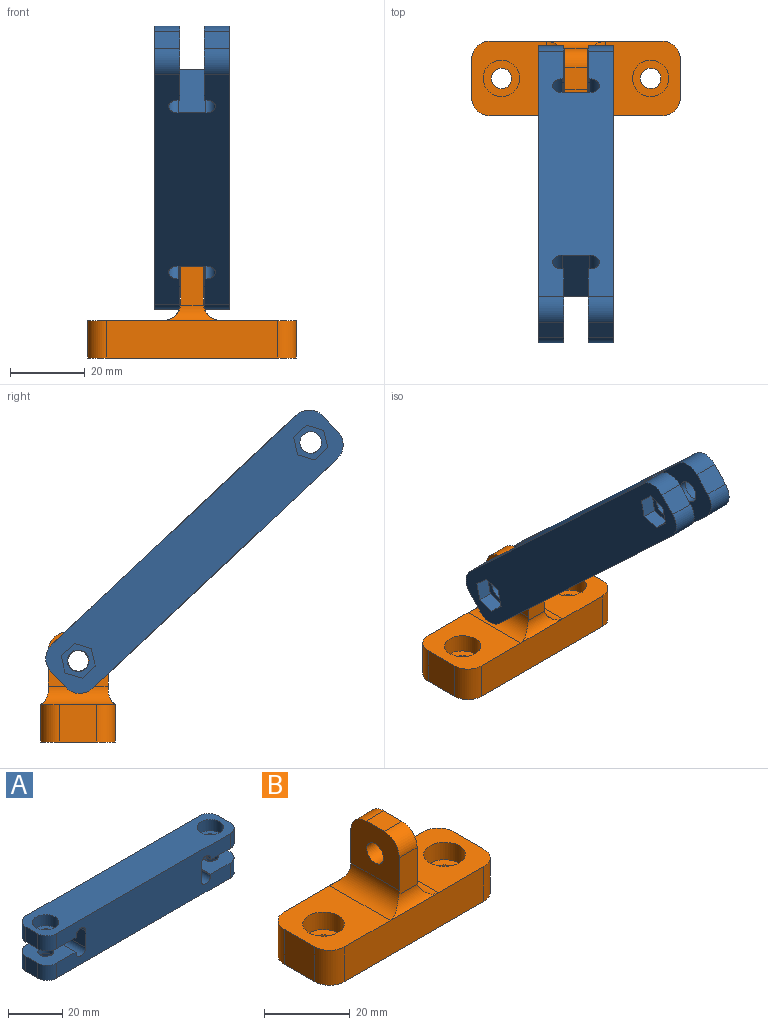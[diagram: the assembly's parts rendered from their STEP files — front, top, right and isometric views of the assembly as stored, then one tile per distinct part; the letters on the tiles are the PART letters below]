
ASSEMBLY  parts=2 mates=1
PART A: 52 faces, bbox 100x16x20 mm
  f0: plane 100x16mm, normal (0,0,-1), area 1459.2mm2, adj f4,f8,f9,f10,f11,f12,f14,f17
  f1: cylinder r=2.9mm len=5.8mm, axis (0,0,1), area 50.1mm2, adj f23,f51
  f2: cylinder r=2.9mm len=5.8mm, axis (0,0,1), area 50.1mm2, adj f18,f44
  f3: plane 6.75x6mm, normal (1,0,0), area 40.5mm2, adj f5,f6,f13,f27
  f4: plane 90x20mm, normal (0,1,0), area 1555.7mm2, adj f0,f5,f9,f13,f14,f15,f18,f19
  f5: cylinder r=5mm len=6.75mm, axis (0,0,1), area 53mm2, adj f3,f4,f13,f27
  f6: cylinder r=5mm len=6.75mm, axis (0,0,-1), area 53mm2, adj f3,f8,f13,f27
  f7: plane 6.75x6mm, normal (-1,0,0), area 40.5mm2, adj f13,f15,f16,f19
  f8: plane 90x20mm, normal (0,-1,0), area 1555.7mm2, adj f0,f6,f10,f13,f16,f17,f18,f19
  f9: cylinder r=5mm len=6.75mm, axis (0,0,-1), area 53mm2, adj f0,f4,f12,f18
  f10: cylinder r=5mm len=6.75mm, axis (0,0,1), area 53mm2, adj f0,f8,f12,f18
  f11: plane 6.75x6mm, normal (1,0,0), area 40.5mm2, adj f0,f14,f17,f23
  f12: plane 6.75x6mm, normal (-1,0,0), area 40.5mm2, adj f0,f9,f10,f18
  f13: plane 100x16mm, normal (0,0,1), area 1429.2mm2, adj f3,f4,f5,f6,f7,f8,f15,f16
  f14: cylinder r=5mm len=6.75mm, axis (0,0,1), area 53mm2, adj f0,f4,f11,f23
  f15: cylinder r=5mm len=6.75mm, axis (0,0,-1), area 53mm2, adj f4,f7,f13,f19
  f16: cylinder r=5mm len=6.75mm, axis (0,0,1), area 53mm2, adj f7,f8,f13,f19
  f17: cylinder r=5mm len=6.75mm, axis (0,0,-1), area 53mm2, adj f0,f8,f11,f23
  f18: plane 16x15mm, normal (0,0,1), area 202.8mm2, adj f2,f4,f8,f9,f10,f12,f22
  f19: plane 16x15mm, normal (0,0,-1), area 202.8mm2, adj f4,f7,f8,f15,f16,f20,f33
  f20: plane 16x0.5mm, normal (1,0,0), area 8mm2, adj f4,f8,f19,f36
  f21: plane 16x7.5mm, normal (-1,0,0), area 120mm2, adj f4,f8,f36,f37
  f22: plane 16x0.5mm, normal (1,0,0), area 8mm2, adj f4,f8,f18,f37
  f23: plane 16x15mm, normal (0,0,1), area 202.8mm2, adj f1,f4,f8,f11,f14,f17,f24
  f24: plane 16x0.5mm, normal (-1,0,0), area 8mm2, adj f4,f8,f23,f35
  f25: plane 16x7.5mm, normal (1,0,0), area 120mm2, adj f4,f8,f34,f35
  f26: plane 16x0.5mm, normal (-1,0,0), area 8mm2, adj f4,f8,f27,f34
  f27: plane 16x15mm, normal (0,0,-1), area 202.8mm2, adj f3,f4,f5,f6,f8,f26,f30
  f28: cylinder r=4.88mm len=9.75mm, axis (0,0,1), area 153.2mm2, adj f13,f29
  f29: plane 9.75x9.75mm, normal (0,0,1), area 48.2mm2, adj f28,f30
  f30: cylinder r=2.9mm len=5.8mm, axis (0,0,1), area 31.9mm2, adj f27,f29
  f31: cylinder r=4.88mm len=9.75mm, axis (0,0,1), area 153.2mm2, adj f13,f32
  f32: plane 9.75x9.75mm, normal (0,0,1), area 48.2mm2, adj f31,f33
  f33: cylinder r=2.9mm len=5.8mm, axis (0,0,1), area 31.9mm2, adj f19,f32
  f34: cylinder r=2.5mm len=16mm, axis (0,-1,0), area 125.7mm2, adj f4,f8,f25,f26
  f35: cylinder r=2.5mm len=16mm, axis (0,-1,0), area 125.7mm2, adj f4,f8,f24,f25
  f36: cylinder r=2.5mm len=16mm, axis (0,-1,0), area 125.7mm2, adj f4,f8,f20,f21
  f37: cylinder r=2.5mm len=16mm, axis (0,-1,0), area 125.7mm2, adj f4,f8,f21,f22
  f38: plane 4.15x4mm, normal (-0.87,-0.5,0), area 19.2mm2, adj f0,f39,f43,f44
  f39: plane 4.15x4mm, normal (-0.87,0.5,0), area 19.2mm2, adj f0,f38,f40,f44
  f40: plane 4.79x4mm, normal (0,1,0), area 19.2mm2, adj f0,f39,f41,f44
  f41: plane 4.15x4mm, normal (0.87,0.5,0), area 19.2mm2, adj f0,f40,f42,f44
  f42: plane 4.15x4mm, normal (0.87,-0.5,0), area 19.2mm2, adj f0,f41,f43,f44
  f43: plane 4.79x4mm, normal (0,-1,0), area 19.2mm2, adj f0,f38,f42,f44
  f44: plane 9.58x8.3mm, normal (0,0,-1), area 33.2mm2, adj f2,f38,f39,f40,f41,f42,f43
  f45: plane 4.79x4mm, normal (0,1,0), area 19.2mm2, adj f0,f46,f50,f51
  f46: plane 4.15x4mm, normal (0.87,0.5,0), area 19.2mm2, adj f0,f45,f47,f51
  f47: plane 4.15x4mm, normal (0.87,-0.5,0), area 19.2mm2, adj f0,f46,f48,f51
  f48: plane 4.79x4mm, normal (0,-1,0), area 19.2mm2, adj f0,f47,f49,f51
  f49: plane 4.15x4mm, normal (-0.87,-0.5,0), area 19.2mm2, adj f0,f48,f50,f51
  f50: plane 4.15x4mm, normal (-0.87,0.5,0), area 19.2mm2, adj f0,f45,f49,f51
  f51: plane 9.58x8.3mm, normal (0,0,-1), area 33.2mm2, adj f1,f45,f46,f47,f48,f49,f50
PART B: 29 faces, bbox 56x20x29.5 mm
  f0: plane 20.05x20mm, normal (0,0,1), area 315.6mm2, adj f3,f4,f5,f15,f19,f20,f24
  f1: plane 20.05x20mm, normal (0,0,1), area 315.6mm2, adj f2,f3,f5,f12,f18,f21,f27
  f2: plane 10x10mm, normal (-1,0,0), area 100mm2, adj f1,f6,f18,f21
  f3: plane 46x10mm, normal (0,-1,0), area 460mm2, adj f0,f1,f6,f13,f18,f19
  f4: plane 10x10mm, normal (1,0,0), area 100mm2, adj f0,f6,f19,f20
  f5: plane 46x10mm, normal (0,1,0), area 460mm2, adj f0,f1,f6,f14,f20,f21
  f6: plane 56x20mm, normal (0,0,-1), area 1051mm2, adj f2,f3,f4,f5,f18,f19,f20,f21
  f7: plane 16x14.5mm, normal (-1,0,0), area 197.5mm2, adj f8,f10,f11,f12,f16,f17,f28
  f8: plane 10.5x6.1mm, normal (0,-1,0), area 62mm2, adj f7,f9,f12,f13,f15,f16
  f9: plane 16x14.5mm, normal (1,0,0), area 197.5mm2, adj f8,f10,f11,f15,f16,f17,f28
  f10: plane 10.5x6.1mm, normal (0,1,0), area 62mm2, adj f7,f9,f12,f14,f15,f17
  f11: plane 6x5.9mm, normal (0,0,1), area 35.4mm2, adj f7,f9,f16,f17
  f12: cylinder r=5mm len=20mm, axis (0,-1,0), area 138.7mm2, adj f1,f7,f8,f10,f13,f14
  f13: cylinder r=5mm len=15.9mm, axis (-1,0,0), area 41.2mm2, adj f3,f8,f12,f15
  f14: cylinder r=5mm len=15.9mm, axis (-1,0,0), area 41.2mm2, adj f5,f10,f12,f15
  f15: cylinder r=5mm len=20mm, axis (0,1,0), area 138.7mm2, adj f0,f8,f9,f10,f13,f14
  f16: cylinder r=5mm len=5.9mm, axis (-1,0,0), area 46.3mm2, adj f7,f8,f9,f11
  f17: cylinder r=5mm len=5.9mm, axis (1,0,0), area 46.3mm2, adj f7,f9,f10,f11
  f18: cylinder r=5mm len=10mm, axis (0,0,1), area 78.5mm2, adj f1,f2,f3,f6
  f19: cylinder r=5mm len=10mm, axis (0,0,-1), area 78.5mm2, adj f0,f3,f4,f6
  f20: cylinder r=5mm len=10mm, axis (0,0,1), area 78.5mm2, adj f0,f4,f5,f6
  f21: cylinder r=5mm len=10mm, axis (0,0,-1), area 78.5mm2, adj f1,f2,f5,f6
  f22: cylinder r=2.75mm len=5.5mm, axis (0,0,1), area 86.4mm2, adj f6,f23
  f23: plane 9.75x9.75mm, normal (0,0,1), area 50.9mm2, adj f22,f24
  f24: cylinder r=4.88mm len=9.75mm, axis (0,0,1), area 153.2mm2, adj f0,f23
  f25: cylinder r=2.75mm len=5.5mm, axis (0,0,1), area 86.4mm2, adj f6,f26
  f26: plane 9.75x9.75mm, normal (0,0,1), area 50.9mm2, adj f25,f27
  f27: cylinder r=4.88mm len=9.75mm, axis (0,0,1), area 153.2mm2, adj f1,f26
  f28: cylinder r=2.75mm len=5.9mm, axis (-1,0,0), area 101.9mm2, adj f7,f9
PLACE A rot(axis=(-0.68,0.29,-0.68),147.4deg) t=(-39.63,-85.16,53.84)mm
PLACE B t=(-7.33,-1.08,2.82)mm fixed
MATE revolute A.f2 <-> B.f28  axis (1,0,0) through (-32.88,-54,24.57)mm
